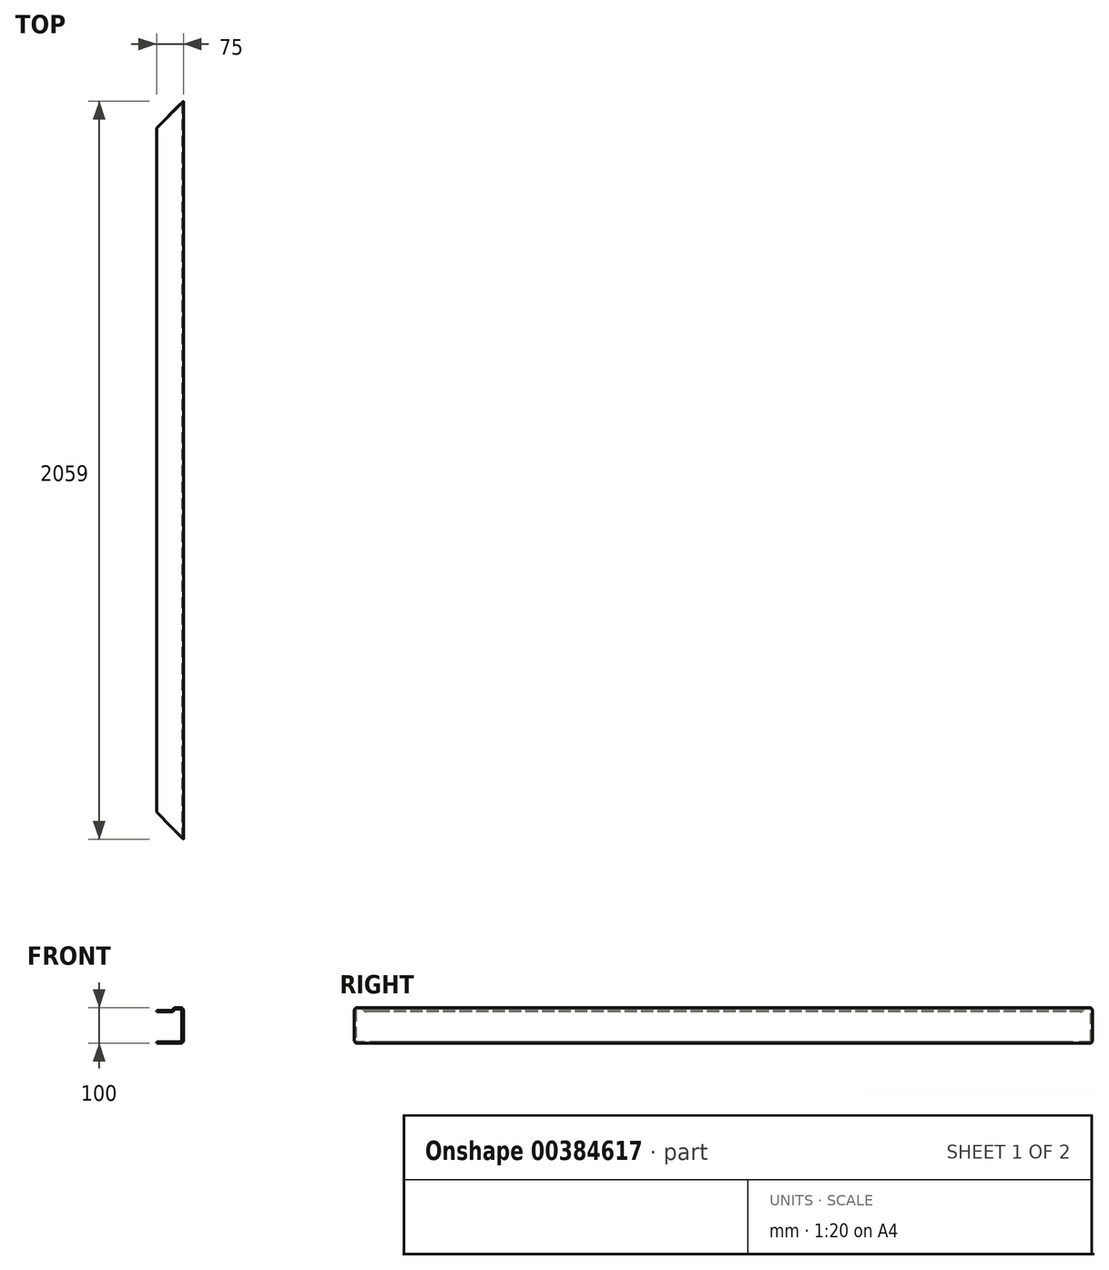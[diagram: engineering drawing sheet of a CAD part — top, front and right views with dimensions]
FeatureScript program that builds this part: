
annotation { "Feature Type Name" : "Feature", "Feature Type Description" : "" }
export const myFeature = defineFeature(function(context is Context, id is Id, definition is map)
    precondition{}
    {
        {
            var Q0;
            Q0=qCreatedBy(makeId("Front.planeOp"),FACE);
            var sketch = newSketch(context, id + "F0", { "sketchPlane" : qUnion([Q0])});
            skLineSegment(sketch, "E0.bottom", {"start": v(-29.5, -50) * mm, "end": v(37.5, -50) * mm});
            skLineSegment(sketch, "E0.top", {"start": v(-29.5, 50) * mm, "end": v(-16.23, 50) * mm});
            skLineSegment(sketch, "E0.left", {"start": v(-37.5, -42) * mm, "end": v(-37.5, 42) * mm});
            skPoint(sketch, "E0.middle", {"position": v(0, 0) * mm});
            skLineSegment(sketch, "E1", {"start": v(-10.1, 47.14) * mm, "end": v(-6.99, 43.43) * mm});
            skLineSegment(sketch, "E2", {"start": v(-3.92, 42) * mm, "end": v(37.5, 42) * mm});
            skLineSegment(sketch, "E3", {"start": v(-3.92, 38) * mm, "end": v(37.5, 38) * mm});
            skPoint(sketch, "E4.orphan", {"position": v(37.5, 50) * mm});
            skPoint(sketch, "E5.orphan", {"position": v(35.5, 48) * mm});
            skLineSegment(sketch, "E6.0", {"start": v(-13.17, 44.57) * mm, "end": v(-10.05, 40.86) * mm});
            skLineSegment(sketch, "E7.0", {"start": v(-29.5, -46) * mm, "end": v(37.5, -46) * mm});
            skLineSegment(sketch, "E8.0", {"start": v(-33.5, -42) * mm, "end": v(-33.5, 42) * mm});
            skLineSegment(sketch, "E9.0", {"start": v(-29.5, 46) * mm, "end": v(-16.23, 46) * mm});
            skPoint(sketch, "E10.orphan", {"position": v(-35.5, 48) * mm});
            skPoint(sketch, "E11.orphan", {"position": v(-35.5, -48) * mm});
            skLineSegment(sketch, "E12", {"start": v(37.5, 42) * mm, "end": v(37.5, 38) * mm});
            skLineSegment(sketch, "E13", {"start": v(37.5, -46) * mm, "end": v(37.5, -50) * mm});
            skPoint(sketch, "E14.visualSharp", {"position": v(-37.5, 50) * mm});
            skArc(sketch, "E14.filletArc", {"start": v(-29.5, 50) * mm, "mid": v(-35.16, 47.66) * mm, "end": v(-37.5, 42) * mm});
            skPoint(sketch, "E15.visualSharp", {"position": v(-33.5, 46) * mm});
            skArc(sketch, "E15.filletArc", {"start": v(-29.5, 46) * mm, "mid": v(-32.33, 44.83) * mm, "end": v(-33.5, 42) * mm});
            skPoint(sketch, "E16.visualSharp", {"position": v(-14.37, 46) * mm});
            skArc(sketch, "E16.filletArc", {"start": v(-13.17, 44.57) * mm, "mid": v(-14.54, 45.63) * mm, "end": v(-16.23, 46) * mm});
            skPoint(sketch, "E17.visualSharp", {"position": v(-12.5, 50) * mm});
            skArc(sketch, "E17.filletArc", {"start": v(-10.1, 47.14) * mm, "mid": v(-12.85, 49.25) * mm, "end": v(-16.23, 50) * mm});
            skPoint(sketch, "E18.visualSharp", {"position": v(-7.65, 38) * mm});
            skArc(sketch, "E18.filletArc", {"start": v(-10.05, 40.86) * mm, "mid": v(-7.3, 38.75) * mm, "end": v(-3.92, 38) * mm});
            skPoint(sketch, "E19.visualSharp", {"position": v(-5.79, 42) * mm});
            skArc(sketch, "E19.filletArc", {"start": v(-6.99, 43.43) * mm, "mid": v(-5.61, 42.37) * mm, "end": v(-3.92, 42) * mm});
            skPoint(sketch, "E20.visualSharp", {"position": v(-33.5, -46) * mm});
            skArc(sketch, "E20.filletArc", {"start": v(-33.5, -42) * mm, "mid": v(-32.33, -44.83) * mm, "end": v(-29.5, -46) * mm});
            skPoint(sketch, "E21.visualSharp", {"position": v(-37.5, -50) * mm});
            skArc(sketch, "E21.filletArc", {"start": v(-37.5, -42) * mm, "mid": v(-35.16, -47.66) * mm, "end": v(-29.5, -50) * mm});
            skSolve(sketch);
        }
        {
            var Q0;
            Q0=makeQuery(id+"F0.imprint","IMPRINT",FACE,{"disambiguationData":[TD([[makeQuery(id+"F0.imprint","IMPRINT",EDGE,{"derivedFrom":sQuery(id+"F0.wireOp",EDGE,"E0.bottom")}),1.0]])]});
            extrude(context, id + "F1", {"entities" : qUnion([Q0]), "oppositeDirection" : true, "depth" : 2059 * mm});
        }
        {
            var Q0;
            Q0=qCreatedBy(makeId("Top.planeOp"),FACE);
            var sketch = newSketch(context, id + "F2", { "sketchPlane" : qUnion([Q0])});
            skLineSegment(sketch, "E22", {"start": v(0, 0) * mm, "end": v(-37.5, 0) * mm});
            skLineSegment(sketch, "E23", {"start": v(0, 0) * mm, "end": v(37.5, 0) * mm});
            skLineSegment(sketch, "E24", {"start": v(37.5, 0) * mm, "end": v(37.5, 75) * mm});
            skLineSegment(sketch, "E25", {"start": v(37.5, 75) * mm, "end": v(-37.5, 0) * mm});
            skSolve(sketch);
        }
        {
            var Q0;
            Q0=sQuery(id+"F0.wireOp",EDGE,"E0.left");
            var Q1;
            Q1=sQuery(id+"F2.wireOp",EDGE,"E25");
            cPlane(context, id + "F3", {"entities" : qUnion([Q0, Q1]), "cplaneType" : CPlaneType.LINE_ANGLE, "offset" : 25 * mm, "angle" : 0 * degree, "width" : 150 * mm, "height" : 150 * mm});
        }
        {
            var Q0;
            Q0=qCreatedBy(id+"F3.planeOp",FACE);
            var sketch = newSketch(context, id + "F4", { "sketchPlane" : qUnion([Q0])});
            skLineSegment(sketch, "E26.bottom", {"start": v(-175, -75) * mm, "end": v(175, -75) * mm});
            skLineSegment(sketch, "E26.top", {"start": v(-175, 75) * mm, "end": v(175, 75) * mm});
            skLineSegment(sketch, "E26.left", {"start": v(-175, -75) * mm, "end": v(-175, 75) * mm});
            skLineSegment(sketch, "E26.right", {"start": v(175, -75) * mm, "end": v(175, 75) * mm});
            skPoint(sketch, "E26.middle", {"position": v(0, 0) * mm});
            skSolve(sketch);
        }
        {
            var Q0;
            Q0=qSketchRegion(id+"F4",true);
            extrude(context, id + "F5", {"entities" : qUnion([Q0]), "operationType" : NewBodyOperationType.REMOVE, "depth" : 150 * mm});
        }
        {
            var Q0;
            Q0=qCreatedBy(makeId("Right.planeOp"),FACE);
            cPlane(context, id + "F6", {"entities" : qUnion([Q0]), "cplaneType" : CPlaneType.OFFSET, "offset" : 200 * mm, "width" : 150 * mm, "height" : 150 * mm});
        }
        {
            var Q0;
            Q0=makeQuery(id+"F1.opExtrude","SWEPT_BODY",BODY,{"disambiguationData":[OSD([sQuery(id+"F0.wireOp",EDGE,"E0.bottom"),sQuery(id+"F0.wireOp",EDGE,"E0.top"),sQuery(id+"F0.wireOp",EDGE,"E0.left"),sQuery(id+"F0.wireOp",EDGE,"E1"),sQuery(id+"F0.wireOp",EDGE,"E2"),sQuery(id+"F0.wireOp",EDGE,"E3"),sQuery(id+"F0.wireOp",EDGE,"E6.0"),sQuery(id+"F0.wireOp",EDGE,"E7.0"),sQuery(id+"F0.wireOp",EDGE,"E8.0"),sQuery(id+"F0.wireOp",EDGE,"E9.0"),sQuery(id+"F0.wireOp",EDGE,"E12"),sQuery(id+"F0.wireOp",EDGE,"E13"),sQuery(id+"F0.wireOp",EDGE,"E14.filletArc"),sQuery(id+"F0.wireOp",EDGE,"E15.filletArc"),sQuery(id+"F0.wireOp",EDGE,"E16.filletArc"),sQuery(id+"F0.wireOp",EDGE,"E17.filletArc"),sQuery(id+"F0.wireOp",EDGE,"E18.filletArc"),sQuery(id+"F0.wireOp",EDGE,"E19.filletArc"),sQuery(id+"F0.wireOp",EDGE,"E20.filletArc"),sQuery(id+"F0.wireOp",EDGE,"E21.filletArc")])]});
            var Q1;
            Q1=qCreatedBy(id+"F6.planeOp",FACE);
            mirror(context, id + "F7", {"entities" : qUnion([Q0]), "mirrorPlane" : qUnion([Q1])});
        }
        {
            var Q0;
            Q0=makeQuery(id+"F1.opExtrude","SWEPT_BODY",BODY,{"disambiguationData":[OSD([sQuery(id+"F0.wireOp",EDGE,"E0.bottom"),sQuery(id+"F0.wireOp",EDGE,"E0.top"),sQuery(id+"F0.wireOp",EDGE,"E0.left"),sQuery(id+"F0.wireOp",EDGE,"E1"),sQuery(id+"F0.wireOp",EDGE,"E2"),sQuery(id+"F0.wireOp",EDGE,"E3"),sQuery(id+"F0.wireOp",EDGE,"E6.0"),sQuery(id+"F0.wireOp",EDGE,"E7.0"),sQuery(id+"F0.wireOp",EDGE,"E8.0"),sQuery(id+"F0.wireOp",EDGE,"E9.0"),sQuery(id+"F0.wireOp",EDGE,"E12"),sQuery(id+"F0.wireOp",EDGE,"E13"),sQuery(id+"F0.wireOp",EDGE,"E14.filletArc"),sQuery(id+"F0.wireOp",EDGE,"E15.filletArc"),sQuery(id+"F0.wireOp",EDGE,"E16.filletArc"),sQuery(id+"F0.wireOp",EDGE,"E17.filletArc"),sQuery(id+"F0.wireOp",EDGE,"E18.filletArc"),sQuery(id+"F0.wireOp",EDGE,"E19.filletArc"),sQuery(id+"F0.wireOp",EDGE,"E20.filletArc"),sQuery(id+"F0.wireOp",EDGE,"E21.filletArc")])]});
            var Q1;
            Q1=qCreatedBy(id+"F6.planeOp",FACE);
            mirror(context, id + "F8", {"operationType" : NewBodyOperationType.ADD, "entities" : qUnion([Q0]), "mirrorPlane" : qUnion([Q1])});
        }
        {
            var Q0;
            Q0=qCreatedBy(id+"F6.planeOp",FACE);
            cPlane(context, id + "F9", {"entities" : qUnion([Q0]), "cplaneType" : CPlaneType.OFFSET, "offset" : 500 * mm, "width" : 150 * mm, "height" : 150 * mm});
        }
        {
            var Q0;
            Q0=makeQuery(id+"F1.opExtrude","SWEPT_BODY",BODY,{"disambiguationData":[OSD([sQuery(id+"F0.wireOp",EDGE,"E0.bottom"),sQuery(id+"F0.wireOp",EDGE,"E0.top"),sQuery(id+"F0.wireOp",EDGE,"E0.left"),sQuery(id+"F0.wireOp",EDGE,"E1"),sQuery(id+"F0.wireOp",EDGE,"E2"),sQuery(id+"F0.wireOp",EDGE,"E3"),sQuery(id+"F0.wireOp",EDGE,"E6.0"),sQuery(id+"F0.wireOp",EDGE,"E7.0"),sQuery(id+"F0.wireOp",EDGE,"E8.0"),sQuery(id+"F0.wireOp",EDGE,"E9.0"),sQuery(id+"F0.wireOp",EDGE,"E12"),sQuery(id+"F0.wireOp",EDGE,"E13"),sQuery(id+"F0.wireOp",EDGE,"E14.filletArc"),sQuery(id+"F0.wireOp",EDGE,"E15.filletArc"),sQuery(id+"F0.wireOp",EDGE,"E16.filletArc"),sQuery(id+"F0.wireOp",EDGE,"E17.filletArc"),sQuery(id+"F0.wireOp",EDGE,"E18.filletArc"),sQuery(id+"F0.wireOp",EDGE,"E19.filletArc"),sQuery(id+"F0.wireOp",EDGE,"E20.filletArc"),sQuery(id+"F0.wireOp",EDGE,"E21.filletArc")])]});
            var Q1;
            Q1=qCreatedBy(id+"F9.planeOp",FACE);
            mirror(context, id + "F10", {"entities" : qUnion([Q0]), "mirrorPlane" : qUnion([Q1])});
        }
        {
            var Q0;
            Q0=makeQuery(id+"F1.opExtrude","SWEPT_BODY",BODY,{"disambiguationData":[OSD([sQuery(id+"F0.wireOp",EDGE,"E0.bottom"),sQuery(id+"F0.wireOp",EDGE,"E0.top"),sQuery(id+"F0.wireOp",EDGE,"E0.left"),sQuery(id+"F0.wireOp",EDGE,"E1"),sQuery(id+"F0.wireOp",EDGE,"E2"),sQuery(id+"F0.wireOp",EDGE,"E3"),sQuery(id+"F0.wireOp",EDGE,"E6.0"),sQuery(id+"F0.wireOp",EDGE,"E7.0"),sQuery(id+"F0.wireOp",EDGE,"E8.0"),sQuery(id+"F0.wireOp",EDGE,"E9.0"),sQuery(id+"F0.wireOp",EDGE,"E12"),sQuery(id+"F0.wireOp",EDGE,"E13"),sQuery(id+"F0.wireOp",EDGE,"E14.filletArc"),sQuery(id+"F0.wireOp",EDGE,"E15.filletArc"),sQuery(id+"F0.wireOp",EDGE,"E16.filletArc"),sQuery(id+"F0.wireOp",EDGE,"E17.filletArc"),sQuery(id+"F0.wireOp",EDGE,"E18.filletArc"),sQuery(id+"F0.wireOp",EDGE,"E19.filletArc"),sQuery(id+"F0.wireOp",EDGE,"E20.filletArc"),sQuery(id+"F0.wireOp",EDGE,"E21.filletArc")])]});
            deleteBodies(context, id + "F11", {"entities" : qUnion([Q0])});
        }
        {
            var Q0;
            Q0=makeQuery(id+"F7.opPattern","COPY",BODY,{"derivedFrom":makeQuery(id+"F1.opExtrude","SWEPT_BODY",BODY,{"disambiguationData":[OSD([sQuery(id+"F0.wireOp",EDGE,"E0.bottom"),sQuery(id+"F0.wireOp",EDGE,"E0.top"),sQuery(id+"F0.wireOp",EDGE,"E0.left"),sQuery(id+"F0.wireOp",EDGE,"E1"),sQuery(id+"F0.wireOp",EDGE,"E2"),sQuery(id+"F0.wireOp",EDGE,"E3"),sQuery(id+"F0.wireOp",EDGE,"E6.0"),sQuery(id+"F0.wireOp",EDGE,"E7.0"),sQuery(id+"F0.wireOp",EDGE,"E8.0"),sQuery(id+"F0.wireOp",EDGE,"E9.0"),sQuery(id+"F0.wireOp",EDGE,"E12"),sQuery(id+"F0.wireOp",EDGE,"E13"),sQuery(id+"F0.wireOp",EDGE,"E14.filletArc"),sQuery(id+"F0.wireOp",EDGE,"E15.filletArc"),sQuery(id+"F0.wireOp",EDGE,"E16.filletArc"),sQuery(id+"F0.wireOp",EDGE,"E17.filletArc"),sQuery(id+"F0.wireOp",EDGE,"E18.filletArc"),sQuery(id+"F0.wireOp",EDGE,"E19.filletArc"),sQuery(id+"F0.wireOp",EDGE,"E20.filletArc"),sQuery(id+"F0.wireOp",EDGE,"E21.filletArc")])]}),"instanceName":"1"});
            deleteBodies(context, id + "F12", {"entities" : qUnion([Q0])});
        }
        {
            var Q0;
            Q0=makeQuery(id+"F10.opPattern","COPY",FACE,{"derivedFrom":makeQuery(id+"F1.opExtrude","SWEPT_FACE",FACE,{"disambiguationData":[OSD([sQuery(id+"F0.wireOp",EDGE,"E7.0")])]}),"instanceName":"1"});
            var sketch = newSketch(context, id + "F13", { "sketchPlane" : qUnion([Q0])});
            skLineSegment(sketch, "E27", {"start": v(1362.5, 2059) * mm, "end": v(1437.5, 2059) * mm});
            skLineSegment(sketch, "E28", {"start": v(1437.5, 2059) * mm, "end": v(1362.5, 1984) * mm});
            skLineSegment(sketch, "E29", {"start": v(1362.5, 2059) * mm, "end": v(1362.5, 1984) * mm});
            skSolve(sketch);
        }
        {
            var Q0;
            Q0=makeQuery(id+"F10.opPattern","COPY",EDGE,{"derivedFrom":makeQuery(id+"F1.opExtrude","CAP_EDGE",EDGE,{"disambiguationData":[OSD([sQuery(id+"F0.wireOp",EDGE,"E0.left")])],"isStart":false}),"instanceName":"1"});
            var Q1;
            Q1=sQuery(id+"F13.wireOp",EDGE,"E28");
            cPlane(context, id + "F14", {"entities" : qUnion([Q0, Q1]), "cplaneType" : CPlaneType.LINE_ANGLE, "offset" : 25 * mm, "angle" : 0 * degree, "width" : 150 * mm, "height" : 150 * mm});
        }
        {
            var Q0;
            Q0=qCreatedBy(id+"F14.planeOp",FACE);
            var sketch = newSketch(context, id + "F15", { "sketchPlane" : qUnion([Q0])});
            skLineSegment(sketch, "E30.bottom", {"start": v(2522.22, -49.99) * mm, "end": v(2267.07, -49.99) * mm});
            skLineSegment(sketch, "E30.top", {"start": v(2522.22, 72.34) * mm, "end": v(2267.07, 72.34) * mm});
            skLineSegment(sketch, "E30.left", {"start": v(2522.22, -49.99) * mm, "end": v(2522.22, 72.34) * mm});
            skLineSegment(sketch, "E30.right", {"start": v(2267.07, -49.99) * mm, "end": v(2267.07, 72.34) * mm});
            skSolve(sketch);
        }
        {
            var Q0;
            Q0=makeQuery(id+"F15.imprint","IMPRINT",FACE,{"disambiguationData":[TD([[makeQuery(id+"F15.imprint","IMPRINT",EDGE,{"derivedFrom":sQuery(id+"F15.wireOp",EDGE,"E30.bottom")}),-1.0]])]});
            extrude(context, id + "F16", {"entities" : qUnion([Q0]), "operationType" : NewBodyOperationType.REMOVE, "oppositeDirection" : true, "depth" : 200 * mm, "hasDraft" : true, "draftAngle" : 3 * degree});
        }
    });
